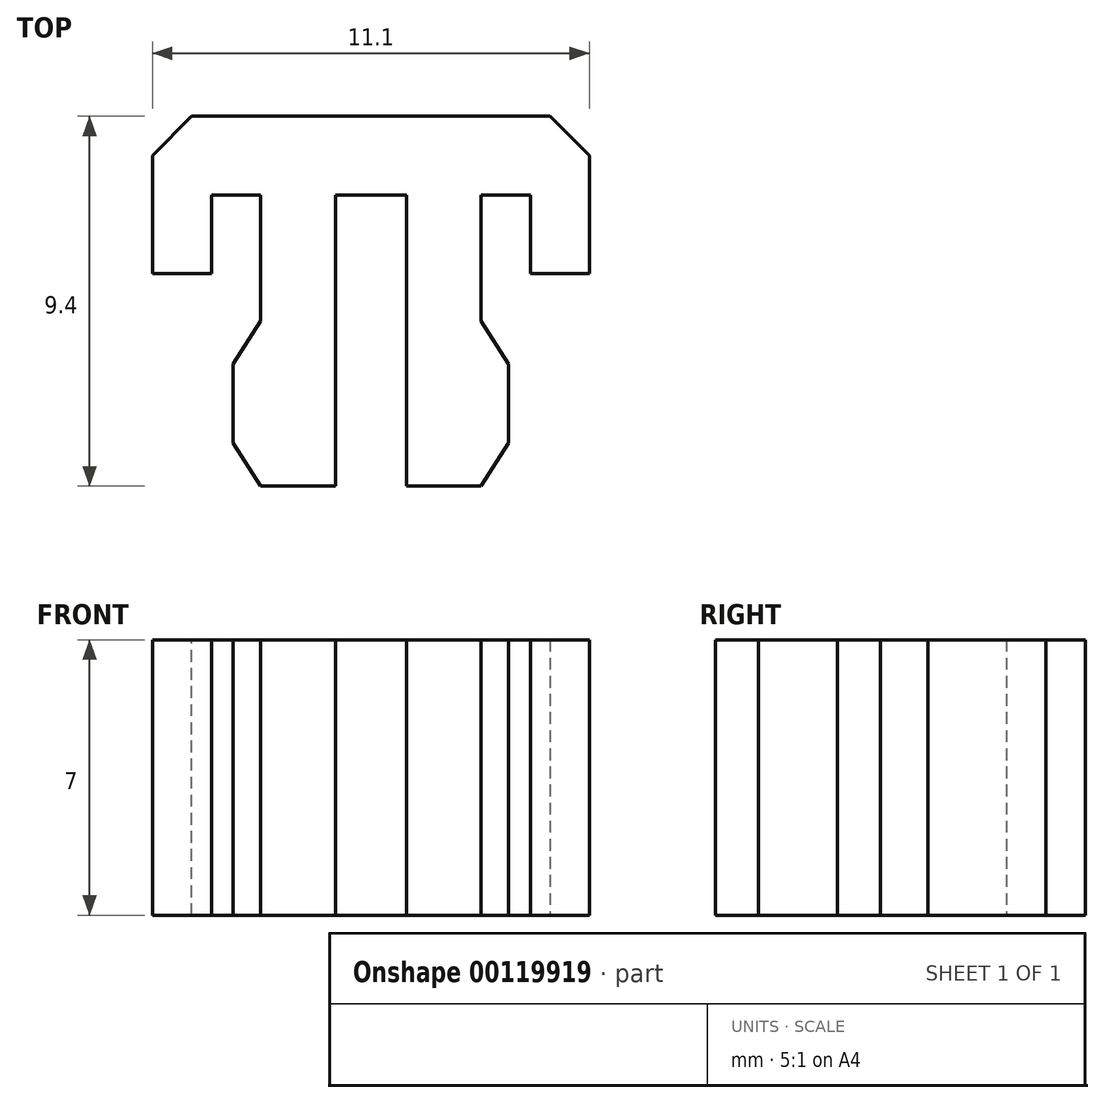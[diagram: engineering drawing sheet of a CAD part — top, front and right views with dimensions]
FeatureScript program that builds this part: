
annotation { "Feature Type Name" : "Feature", "Feature Type Description" : "" }
export const myFeature = defineFeature(function(context is Context, id is Id, definition is map)
    precondition{}
    {
        {
            var Q0;
            Q0=qCreatedBy(makeId("Top.planeOp"),FACE);
            var sketch = newSketch(context, id + "F0", { "sketchPlane" : qUnion([Q0])});
            skLineSegment(sketch, "E0.bottom", {"start": v(-0.9, 0) * mm, "end": v(-2.8, 0) * mm});
            skLineSegment(sketch, "E0.top", {"start": v(-0.9, -7.4) * mm, "end": v(-2.8, -7.4) * mm});
            skLineSegment(sketch, "E0.left", {"start": v(-0.9, 0) * mm, "end": v(-0.9, -7.4) * mm});
            skLineSegment(sketch, "E0.right", {"start": v(-2.8, 0) * mm, "end": v(-2.8, -7.4) * mm});
            skLineSegment(sketch, "E1", {"start": v(-2.8, -7.4) * mm, "end": v(-3.5, -6.3) * mm});
            skLineSegment(sketch, "E2", {"start": v(-3.5, -6.3) * mm, "end": v(-3.5, -4.3) * mm});
            skLineSegment(sketch, "E3", {"start": v(-3.5, -4.3) * mm, "end": v(-2.8, -3.2) * mm});
            skLineSegment(sketch, "E4", {"start": v(-2.8, 0) * mm, "end": v(-4.05, 0) * mm});
            skLineSegment(sketch, "E5", {"start": v(-4.05, 0) * mm, "end": v(-4.05, -2) * mm});
            skLineSegment(sketch, "E6", {"start": v(-4.05, -2) * mm, "end": v(-5.55, -2) * mm});
            skLineSegment(sketch, "E7", {"start": v(-5.55, -2) * mm, "end": v(-5.55, 2) * mm});
            skLineSegment(sketch, "E8", {"start": v(-5.55, 2) * mm, "end": v(0, 2) * mm});
            skLineSegment(sketch, "E9.MirrorCS", {"start": v(2.8, 0) * mm, "end": v(2.8, -7.4) * mm});
            skLineSegment(sketch, "E10.MirrorCS", {"start": v(0.9, 0) * mm, "end": v(0.9, -7.4) * mm});
            skLineSegment(sketch, "E11.MirrorCS", {"start": v(0.9, 0) * mm, "end": v(2.8, 0) * mm});
            skLineSegment(sketch, "E12.MirrorCS", {"start": v(5.55, -2) * mm, "end": v(5.55, 2) * mm});
            skLineSegment(sketch, "E13.MirrorCS", {"start": v(3.5, -4.3) * mm, "end": v(2.8, -3.2) * mm});
            skLineSegment(sketch, "E14.MirrorCS", {"start": v(0.9, -7.4) * mm, "end": v(2.8, -7.4) * mm});
            skLineSegment(sketch, "E15.MirrorCS", {"start": v(5.55, 2) * mm, "end": v(0, 2) * mm});
            skLineSegment(sketch, "E16.MirrorCS", {"start": v(2.8, -7.4) * mm, "end": v(3.5, -6.3) * mm});
            skLineSegment(sketch, "E17.MirrorCS", {"start": v(2.8, 0) * mm, "end": v(4.05, 0) * mm});
            skLineSegment(sketch, "E18.MirrorCS", {"start": v(3.5, -6.3) * mm, "end": v(3.5, -4.3) * mm});
            skLineSegment(sketch, "E19.MirrorCS", {"start": v(4.05, -2) * mm, "end": v(5.55, -2) * mm});
            skLineSegment(sketch, "E20.MirrorCS", {"start": v(4.05, 0) * mm, "end": v(4.05, -2) * mm});
            skLineSegment(sketch, "E21", {"start": v(-0.9, 0) * mm, "end": v(0.9, 0) * mm});
            skSolve(sketch);
        }
        {
            var Q0;
            Q0 = qSketchRegion(id + "F0", true);
            extrude(context, id + "F1", {"entities" : qUnion([Q0]), "depth" : 7 * mm});
        }
        {
            var Q0;
            Q0=makeQuery(id+"F1.opExtrude","SWEPT_EDGE",EDGE,{"disambiguationData":[OSD([sQuery(id+"F0.wireOp",EDGE,"E7"),sQuery(id+"F0.wireOp",EDGE,"E8")])]});
            var Q1;
            Q1=makeQuery(id+"F1.opExtrude","SWEPT_EDGE",EDGE,{"disambiguationData":[OSD([sQuery(id+"F0.wireOp",EDGE,"E12.MirrorCS"),sQuery(id+"F0.wireOp",EDGE,"E15.MirrorCS")])]});
            chamfer(context, id + "F2", {"entities" : qUnion([Q0, Q1]), "width" : 1 * mm, "tangentPropagation" : true});
        }
    });
